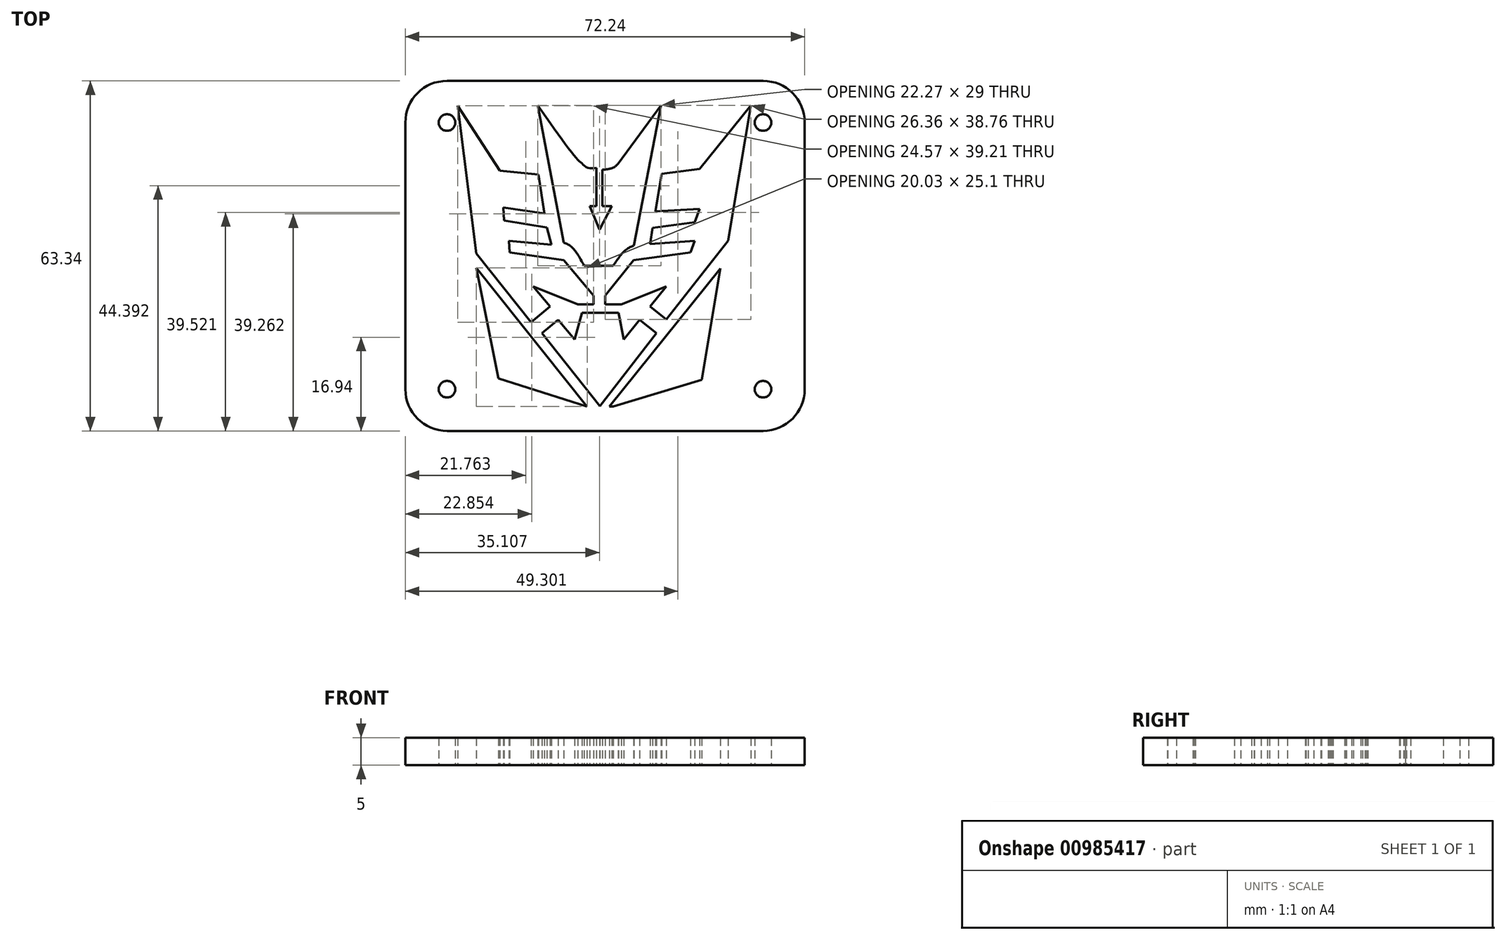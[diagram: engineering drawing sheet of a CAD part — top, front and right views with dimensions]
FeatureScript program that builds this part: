
annotation { "Feature Type Name" : "Feature", "Feature Type Description" : "" }
export const myFeature = defineFeature(function(context is Context, id is Id, definition is map)
    precondition{}
    {
        {
            var Q0;
            Q0=qCreatedBy(makeId("Top.planeOp"),FACE);
            var sketch = newSketch(context, id + "F0", { "sketchPlane" : qUnion([Q0])});
            skPoint(sketch, "E0.middle", {"position": v(0, 0) * mm});
            skLineSegment(sketch, "E1.bottom", {"start": v(-28.57, 31.67) * mm, "end": v(28.58, 31.67) * mm});
            skLineSegment(sketch, "E1.top", {"start": v(-28.57, -31.67) * mm, "end": v(28.58, -31.67) * mm});
            skLineSegment(sketch, "E1.left", {"start": v(-36.12, 24.13) * mm, "end": v(-36.12, -24.13) * mm});
            skLineSegment(sketch, "E1.right", {"start": v(36.12, 24.13) * mm, "end": v(36.12, -24.13) * mm});
            skPoint(sketch, "E2.visualSharp", {"position": v(-36.11, 31.67) * mm});
            skArc(sketch, "E2.filletArc", {"start": v(-28.57, 31.67) * mm, "mid": v(-33.9, 29.46) * mm, "end": v(-36.11, 24.13) * mm});
            skPoint(sketch, "E3.visualSharp", {"position": v(36.12, 31.67) * mm});
            skArc(sketch, "E3.filletArc", {"start": v(36.12, 24.13) * mm, "mid": v(33.9, 29.46) * mm, "end": v(28.58, 31.67) * mm});
            skPoint(sketch, "E4.visualSharp", {"position": v(36.12, -31.67) * mm});
            skArc(sketch, "E4.filletArc", {"start": v(28.58, -31.67) * mm, "mid": v(33.9, -29.46) * mm, "end": v(36.12, -24.13) * mm});
            skPoint(sketch, "E5.visualSharp", {"position": v(-36.12, -31.67) * mm});
            skArc(sketch, "E5.filletArc", {"start": v(-36.11, -24.13) * mm, "mid": v(-33.9, -29.46) * mm, "end": v(-28.57, -31.67) * mm});
            skCircle(sketch, "E6", {"center": v(28.58, 24.13) * mm, "radius": 1.5 * mm});
            skCircle(sketch, "E7", {"center": v(-28.57, 24.13) * mm, "radius": 1.5 * mm});
            skCircle(sketch, "E8", {"center": v(-28.57, -24.13) * mm, "radius": 1.5 * mm});
            skCircle(sketch, "E9", {"center": v(28.58, -24.13) * mm, "radius": 1.5 * mm});
            skLineSegment(sketch, "E10", {"start": v(20.84, -2.3) * mm, "end": v(17.51, -22.45) * mm});
            skLineSegment(sketch, "E11", {"start": v(17.51, -22.45) * mm, "end": v(1.5, -27.23) * mm});
            skLineSegment(sketch, "E12", {"start": v(20.84, -2.3) * mm, "end": v(0.77, -27.23) * mm});
            skLineSegment(sketch, "E13", {"start": v(1.5, -27.23) * mm, "end": v(0.77, -27.23) * mm});
            skLineSegment(sketch, "E14", {"start": v(9.28, -14) * mm, "end": v(6.25, -11.57) * mm});
            skLineSegment(sketch, "E15", {"start": v(6.25, -11.57) * mm, "end": v(3.75, -14.68) * mm});
            skLineSegment(sketch, "E16", {"start": v(3.75, -14.68) * mm, "end": v(3.37, -15.15) * mm});
            skLineSegment(sketch, "E17", {"start": v(3.37, -15.15) * mm, "end": v(2.46, -10.32) * mm});
            skLineSegment(sketch, "E18", {"start": v(2.46, -10.32) * mm, "end": v(-4.18, -10.32) * mm});
            skLineSegment(sketch, "E19", {"start": v(-4.18, -10.32) * mm, "end": v(-5.51, -15.15) * mm});
            skLineSegment(sketch, "E20", {"start": v(-5.51, -15.15) * mm, "end": v(-8.51, -11.57) * mm});
            skLineSegment(sketch, "E21", {"start": v(-8.51, -11.57) * mm, "end": v(-11.42, -14) * mm});
            skLineSegment(sketch, "E22", {"start": v(-13.36, -12.01) * mm, "end": v(-9.95, -9.15) * mm});
            skLineSegment(sketch, "E23", {"start": v(-9.98, -9.15) * mm, "end": v(-13.02, -5.52) * mm});
            skLineSegment(sketch, "E24", {"start": v(-13.02, -5.52) * mm, "end": v(-4.9, -8.75) * mm});
            skLineSegment(sketch, "E25", {"start": v(-4.9, -8.75) * mm, "end": v(-2.07, -8.75) * mm});
            skLineSegment(sketch, "E26", {"start": v(-2.07, -8.75) * mm, "end": v(-2.07, -7.19) * mm});
            skLineSegment(sketch, "E27", {"start": v(-2.07, -7.19) * mm, "end": v(-7.44, -0.77) * mm});
            skLineSegment(sketch, "E28", {"start": v(-7.44, -0.77) * mm, "end": v(-17.23, 0.6) * mm});
            skLineSegment(sketch, "E29", {"start": v(11.08, -11.53) * mm, "end": v(8.13, -9.15) * mm});
            skLineSegment(sketch, "E30", {"start": v(8.13, -9.15) * mm, "end": v(11.06, -5.52) * mm});
            skLineSegment(sketch, "E31", {"start": v(11.06, -5.52) * mm, "end": v(2.94, -8.75) * mm});
            skLineSegment(sketch, "E32", {"start": v(2.94, -8.75) * mm, "end": v(0, -8.75) * mm});
            skLineSegment(sketch, "E33", {"start": v(0, -8.75) * mm, "end": v(0, -7.19) * mm});
            skLineSegment(sketch, "E34", {"start": v(0, -7.19) * mm, "end": v(5.16, -0.77) * mm});
            skLineSegment(sketch, "E35", {"start": v(5.16, -0.77) * mm, "end": v(15.44, 0.6) * mm});
            skLineSegment(sketch, "E36", {"start": v(15.44, 0.6) * mm, "end": v(16.22, 2.72) * mm});
            skLineSegment(sketch, "E37", {"start": v(16.22, 2.72) * mm, "end": v(8.13, 2.17) * mm});
            skLineSegment(sketch, "E38", {"start": v(8.13, 2.17) * mm, "end": v(8.6, 5.04) * mm});
            skLineSegment(sketch, "E39", {"start": v(8.6, 5.04) * mm, "end": v(16.22, 6.06) * mm});
            skLineSegment(sketch, "E40", {"start": v(16.22, 6.06) * mm, "end": v(17.13, 8.5) * mm});
            skLineSegment(sketch, "E41", {"start": v(17.13, 8.5) * mm, "end": v(9.1, 8.03) * mm});
            skLineSegment(sketch, "E42", {"start": v(9.1, 8.03) * mm, "end": v(10.22, 14.84) * mm});
            skLineSegment(sketch, "E43", {"start": v(10.22, 14.84) * mm, "end": v(17.13, 15.76) * mm});
            skLineSegment(sketch, "E44", {"start": v(17.13, 15.76) * mm, "end": v(26.36, 27.23) * mm});
            skLineSegment(sketch, "E45", {"start": v(26.36, 27.23) * mm, "end": v(22.26, 2.72) * mm});
            skLineSegment(sketch, "E46", {"start": v(22.26, 2.72) * mm, "end": v(11.08, -11.53) * mm});
            skLineSegment(sketch, "E47", {"start": v(-17.23, 0.6) * mm, "end": v(-17.35, 2.72) * mm});
            skLineSegment(sketch, "E48", {"start": v(-17.35, 2.72) * mm, "end": v(-9.69, 2) * mm});
            skLineSegment(sketch, "E49", {"start": v(-9.69, 2) * mm, "end": v(-10.55, 5.11) * mm});
            skLineSegment(sketch, "E50", {"start": v(-10.55, 5.11) * mm, "end": v(-18.28, 6.4) * mm});
            skLineSegment(sketch, "E51", {"start": v(-18.28, 6.4) * mm, "end": v(-18.42, 8.77) * mm});
            skLineSegment(sketch, "E52", {"start": v(-18.55, 8.77) * mm, "end": v(-10.98, 7.7) * mm});
            skLineSegment(sketch, "E53", {"start": v(-10.98, 7.7) * mm, "end": v(-12.03, 14.72) * mm});
            skLineSegment(sketch, "E54", {"start": v(-23.31, 0.46) * mm, "end": v(-13.36, -12.01) * mm});
            skLineSegment(sketch, "E55", {"start": v(-3.25, -27.28) * mm, "end": v(-23.28, -2.18) * mm});
            skLineSegment(sketch, "E56", {"start": v(-23.28, -2.18) * mm, "end": v(-19.27, -22.17) * mm});
            skLineSegment(sketch, "E57", {"start": v(-19.27, -22.17) * mm, "end": v(-3.25, -27.28) * mm});
            skLineSegment(sketch, "E58", {"start": v(-12.03, 14.72) * mm, "end": v(-19.04, 15.45) * mm});
            skLineSegment(sketch, "E59", {"start": v(-19.04, 15.45) * mm, "end": v(-19.04, 15.45) * mm});
            skLineSegment(sketch, "E60", {"start": v(-1.54, 15.95) * mm, "end": v(-1.54, 8.98) * mm});
            skLineSegment(sketch, "E61", {"start": v(-1.54, 8.98) * mm, "end": v(-2.77, 8.98) * mm});
            skLineSegment(sketch, "E62", {"start": v(-0.5, 8.98) * mm, "end": v(1.21, 8.98) * mm});
            skLineSegment(sketch, "E63", {"start": v(-0.5, 8.98) * mm, "end": v(-0.5, 15.6) * mm});
            skLineSegment(sketch, "E64", {"start": v(1.48, -1.78) * mm, "end": v(-3.78, -1.78) * mm});
            skLineSegment(sketch, "E65", {"start": v(5.25, 1.95) * mm, "end": v(10.12, 27.22) * mm});
            skLineSegment(sketch, "E66", {"start": v(-7.5, 2.43) * mm, "end": v(-12.15, 27.22) * mm});
            skLineSegment(sketch, "E67", {"start": v(1.21, 8.98) * mm, "end": v(-1.02, 4.79) * mm});
            skLineSegment(sketch, "E68", {"start": v(-2.77, 8.98) * mm, "end": v(-1.02, 4.79) * mm});
            skLineSegment(sketch, "E69", {"start": v(10.12, 27.22) * mm, "end": v(2.4, 16.71) * mm});
            skFitSpline(sketch, "E70", {"points": [v(-1.54, 15.95) * mm, v(-3.15, 15.95) * mm, v(-4.18, 16.74) * mm, v(-5.12, 17.6) * mm, v(-12.15, 27.22) * mm], "startDerivative": vector(-9.43, -1.44) * mm, "endDerivative": vector(-17.51, 25.04) * mm});
            skFitSpline(sketch, "E71", {"points": [v(2.4, 16.71) * mm, v(1.44, 15.95) * mm, v(-0.5, 15.6) * mm], "startDerivative": vector(-1.89, -1.96) * mm, "endDerivative": vector(-3.81, -0.33) * mm});
            skFitSpline(sketch, "E72", {"points": [v(-7.5, 2.43) * mm, v(-5.93, 1.5) * mm, v(-3.78, -1.78) * mm], "startDerivative": vector(3.94, -1.63) * mm, "endDerivative": vector(3.52, -6.48) * mm});
            skFitSpline(sketch, "E73", {"points": [v(5.68, 1.95) * mm, v(3.83, 1.15) * mm, v(1.48, -1.78) * mm], "startDerivative": vector(-4.44, -1.21) * mm, "endDerivative": vector(-3.97, -6) * mm});
            skLineSegment(sketch, "E74", {"start": v(-23.31, 0.46) * mm, "end": v(-26.64, 27.2) * mm});
            skLineSegment(sketch, "E75", {"start": v(-26.64, 27.2) * mm, "end": v(-19.04, 15.45) * mm});
            skLineSegment(sketch, "E76", {"start": v(5.25, 1.95) * mm, "end": v(5.05, 1.58) * mm});
            skLineSegment(sketch, "E77", {"start": v(-11.42, -14) * mm, "end": v(-0.91, -27.18) * mm});
            skLineSegment(sketch, "E78", {"start": v(-0.91, -27.18) * mm, "end": v(9.28, -14) * mm});
            skLineSegment(sketch, "E79", {"start": v(-26.64, 27.2) * mm, "end": v(-23.31, 0.46) * mm});
            skLineSegment(sketch, "E80", {"start": v(-13.02, -5.52) * mm, "end": v(-9.95, -9.15) * mm});
            skLineSegment(sketch, "E81", {"start": v(-18.42, 8.77) * mm, "end": v(-10.98, 7.7) * mm});
            skLineSegment(sketch, "E82", {"start": v(-19.04, 15.45) * mm, "end": v(-26.64, 27.2) * mm});
            skSolve(sketch);
        }
        {
            var Q0;
            Q0 = qSketchRegion(id + "F0", true);
            extrude(context, id + "F1", {"entities" : qUnion([Q0]), "depth" : 5 * mm, "offsetDistance" : 25 * mm});
        }
    });
